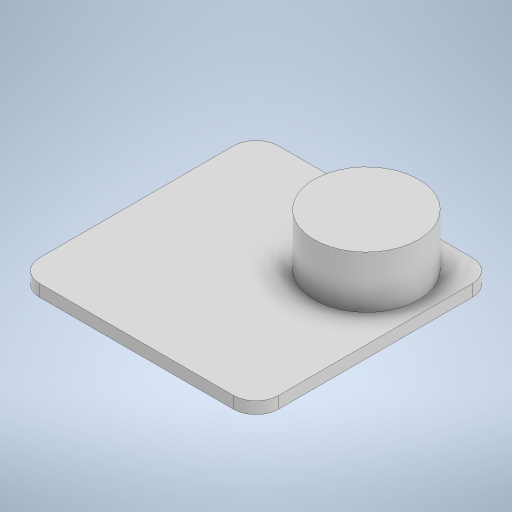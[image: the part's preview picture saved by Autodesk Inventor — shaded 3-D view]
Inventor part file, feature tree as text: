
AUTODESK INVENTOR PART (.ipt)
format: ipt  version: 2024 (Build 280153000, 153)  size: 248,832 bytes
history: native  units: mm
features: extrude x3, sketch x3, other x1, fillet x1
ambient origin geometry x8: Origin, YZ Plane, XZ Plane, XY Plane, X Axis, Y Axis, Z Axis, Center Point
bodies: Body1 (feature_tree)
feature tree (8):
  other  "ソリッド1"
  extrude  "押し出し1"  Depth=32.0mm
  extrude  "押し出し2"  Depth=32.0mm
  extrude  "押し出し4"  Depth=1.6mm TaperAngle=0.0deg
  fillet  "フィレット2"  Radius=14.0mm
  sketch  "スケッチ1"
  sketch  "スケッチ2"
  sketch  "スケッチ5"
